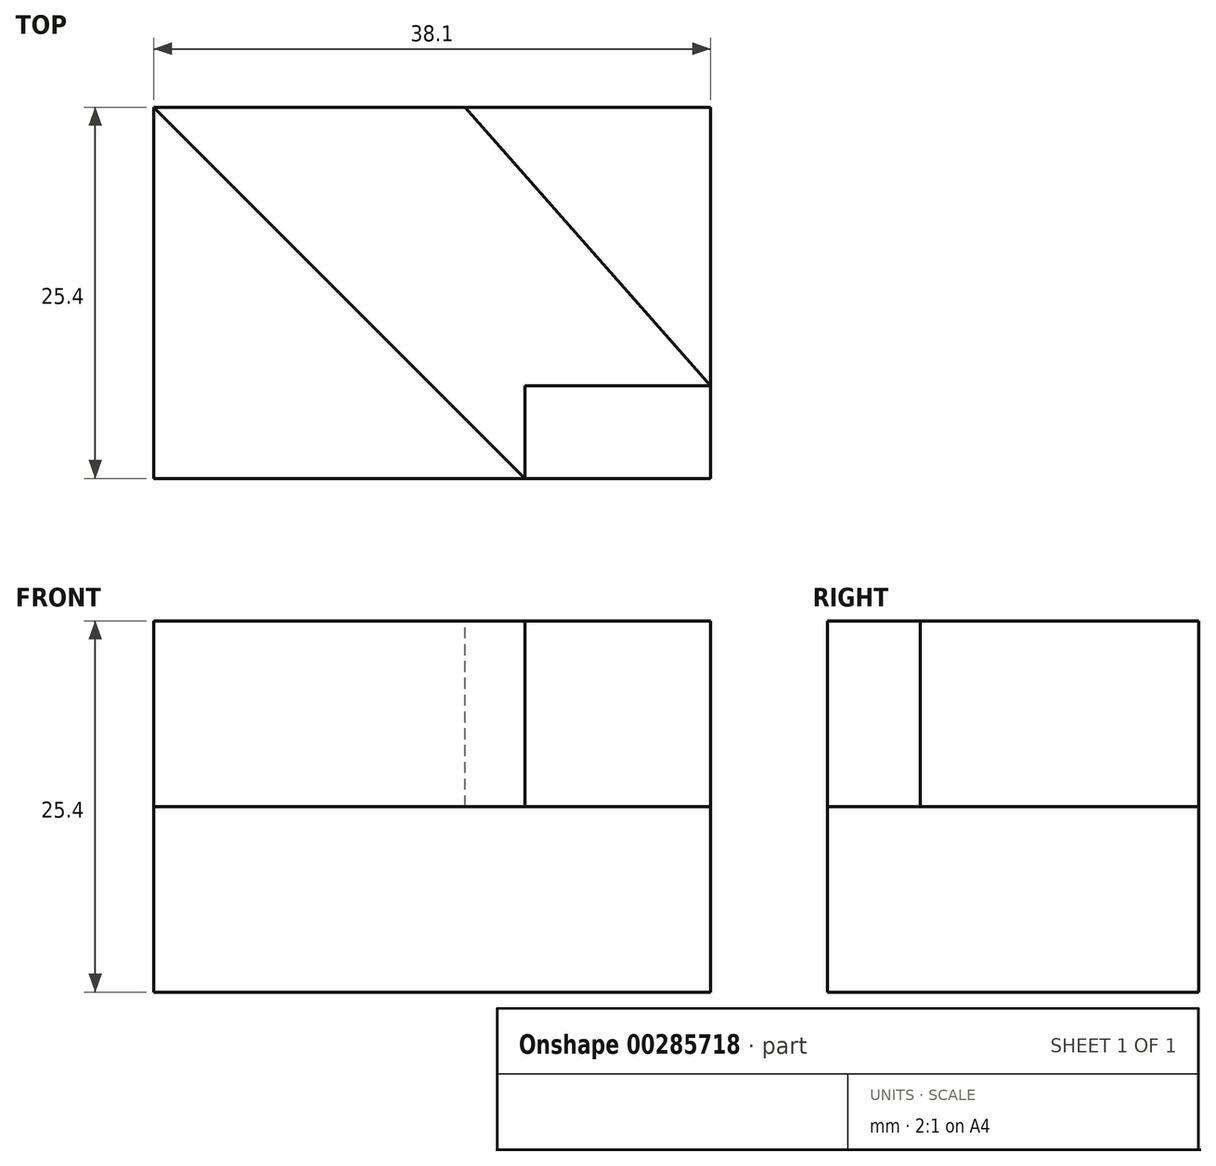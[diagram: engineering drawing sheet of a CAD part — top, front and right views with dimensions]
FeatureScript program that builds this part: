
annotation { "Feature Type Name" : "Feature", "Feature Type Description" : "" }
export const myFeature = defineFeature(function(context is Context, id is Id, definition is map)
    precondition{}
    {
        {
            var Q0;
            Q0=qCreatedBy(makeId("Front.planeOp"),FACE);
            var sketch = newSketch(context, id + "F0", { "sketchPlane" : qUnion([Q0])});
            skLineSegment(sketch, "E0", {"start": v(0, 0) * mm, "end": v(0, 25.4) * mm});
            skLineSegment(sketch, "E1", {"start": v(0, 25.4) * mm, "end": v(38.1, 25.4) * mm});
            skLineSegment(sketch, "E2", {"start": v(38.1, 25.4) * mm, "end": v(38.1, 0) * mm});
            skLineSegment(sketch, "E3", {"start": v(38.1, 0) * mm, "end": v(0, 0) * mm});
            skSolve(sketch);
        }
        {
            var Q0;
            Q0=makeQuery(id+"F0.imprint","IMPRINT",FACE,{"disambiguationData":[TD([[makeQuery(id+"F0.imprint","IMPRINT",EDGE,{"derivedFrom":sQuery(id+"F0.wireOp",EDGE,"E0")}),-1.0]])]});
            extrude(context, id + "F1", {"entities" : qUnion([Q0]), "depth" : 25.4 * mm});
        }
        {
            var Q0;
            Q0=makeQuery(id+"F1.opExtrude","CAP_FACE",FACE,{"disambiguationData":[OSD([sQuery(id+"F0.wireOp",EDGE,"E0"),sQuery(id+"F0.wireOp",EDGE,"E1"),sQuery(id+"F0.wireOp",EDGE,"E2"),sQuery(id+"F0.wireOp",EDGE,"E3")])],"isStart":false});
            var sketch = newSketch(context, id + "F2", { "sketchPlane" : qUnion([Q0])});
            skLineSegment(sketch, "E4", {"start": v(38.1, 25.4) * mm, "end": v(25.4, 25.4) * mm});
            skLineSegment(sketch, "E5", {"start": v(25.4, 25.4) * mm, "end": v(25.4, 12.7) * mm});
            skLineSegment(sketch, "E6", {"start": v(25.4, 12.7) * mm, "end": v(38.1, 12.7) * mm});
            skLineSegment(sketch, "E7", {"start": v(38.1, 12.7) * mm, "end": v(38.1, 25.4) * mm});
            skSolve(sketch);
        }
        {
            var Q0;
            Q0=makeQuery(id+"F2.imprint","IMPRINT",FACE,{"disambiguationData":[TD([[makeQuery(id+"F2.imprint","IMPRINT",EDGE,{"derivedFrom":sQuery(id+"F2.wireOp",EDGE,"E4")}),-1.0]])]});
            extrude(context, id + "F3", {"entities" : qUnion([Q0]), "operationType" : NewBodyOperationType.REMOVE, "oppositeDirection" : true, "depth" : 6.35 * mm});
        }
        {
            var Q0;
            Q0=makeQuery(id+"F1.opExtrude","SWEPT_FACE",FACE,{"disambiguationData":[OSD([sQuery(id+"F0.wireOp",EDGE,"E1")])]});
            var sketch = newSketch(context, id + "F4", { "sketchPlane" : qUnion([Q0])});
            skLineSegment(sketch, "E8", {"start": v(0, 0) * mm, "end": v(25.4, -25.4) * mm});
            skLineSegment(sketch, "E9", {"start": v(38.1, -19.05) * mm, "end": v(21.3, 0) * mm});
            skSolve(sketch);
        }
        {
            var Q0;
            Q0=makeQuery(id+"F4.imprint","IMPRINT",FACE,{"disambiguationData":[TD([[makeQuery(id+"F4.imprint","IMPRINT",EDGE,{"derivedFrom":sQuery(id+"F4.wireOp",EDGE,"E8")}),-1.0]])]});
            var Q1;
            {var subQ0=sQuery(id+"F4.wireOp",EDGE,"E9");Q1=makeQuery(id+"F4.imprint","IMPRINT",FACE,{"disambiguationData":[TD([[makeQuery(id+"F4.imprint","IMPRINT",EDGE,{"derivedFrom":subQ0}),-1.0]])]});}
            extrude(context, id + "F5", {"entities" : qUnion([Q0, Q1]), "operationType" : NewBodyOperationType.REMOVE, "endBound" : BoundingType.SYMMETRIC, "oppositeDirection" : true, "depth" : 25.4 * mm});
        }
    });
